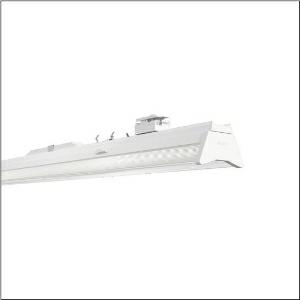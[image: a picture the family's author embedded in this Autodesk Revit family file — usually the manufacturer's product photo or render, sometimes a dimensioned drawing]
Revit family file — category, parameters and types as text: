
# Revit family: licross_21_performance_mo_52td16dn66xg
name_source: partatom
category: Lighting Fixtures
units: mm (PartAtom-declared; Revit-internal decimal feet)

## family parameters
Cut with Voids When Loaded = No
Host = Face
Light Source = No
Part Type = Normal
Room Calculation Point = No
Round Connector Dimension = Use Diameter
Shared = No

## types (1)
- --- (1 x LED, 6000 lm, 33.8 W, 6500K)
    Apparent Load = 34 VA
    CIE Flux Codes = 66 88 96 79 100
    Color Rendering = 80
    Color Temperature = 6500K
    Default Elevation = 1800 mm
    Description = Licross 21 Performance MO, luminaire insert, of sheet steel, galvanised, coil coated, white, length: 1.500mm, width: 120mm, height: 123mm, LED rated luminous flux: 6.000lm, light colour: 865, SDCM (Standard Deviation of Colour Matching)MacAdam ≤ 3 SDCM (initial), control gear: DALI 2, with plug, 5-pole, with phase selection, mains connection: 220..240V, AC, 50/60Hz, rated input power: 34W, internal wiring halogen-free, primary light control with lens, of plastic, primary optical cover: cover, of PMMA, light emission: direct/indirect distribution, primary light characteristic: symmetric, protection rating (complete): IP54, insulation class (complete): insulation class I (protective earthing), certification: CE, ENEC, VDE, UKCA, protection symbol: D if used in an environment with non-conductive dust loads with corresponding accessories, impact resistance: IK06, permissible ambient temperature for indoor applications: -25..+45°C, corresponds to IFS (International Featured Standards) requirements for safety and quality in the food industry, reducing of maximum allowable ambient temperature of 5°C with ceiling mounting, LABS conformity tested according to VDMA 24364:2018-05, The light source and the operating device comply with the requirements of the Ecodesign Regulation (EU) 2019/2020 and are replaceable in accordance with this regulation, packaging unit: 1 piece
    Height = 114 mm
    Lamp = 1 x LED
    Lamp Light Flux = 6000 lm
    Lamp Power = 33.8 W
    Lamp count = 1
    Length = 1500 mm
    Luminous efficacy = 178 lm/W
    Manufacturer = Siteco
    ModVariant = No
    Model = 52TD16DN66XG
    Mounting Place = Ceiling
    Mounting Type = Pendant
    Number of Poles = 1
    OnlyDefault = Yes
    Power Factor = 1
    Product Name = Licross 21 Performance MO
    Product group = luminaire insert | ceiling pendant
    ProductGroupID = 901
    Protection Class = Protection class I
    Protection Degree = IP 54
    RLX_Detail_Level = 1
    RLX_Emergency_Light_Flux = 0 lm
    RLX_Emergency_Type = 0
    RLX_Emergency_Type_DB = No
    RlxData = <blob elided: 33937 chars, md5=2f7d9282>
    Socket = socket
    Standby Power = 0 W
    System Light Flux = 6000 lm
    System Power = 34 W
    Type Comments = factory setting: luminous flux: 100 % | dim-lin: 254 | 229 mA
    Type Image = l_1256138.jpg
    URL = http://relux.com
    VarID = @adj_037559
    Voltage = 0 V
    Weight = 0.00 kg
    Width = 120 mm

## geometry (parser evidence)
native form markers: Blend x4, Sweep x12
no freeform markers — native parametric forms only
